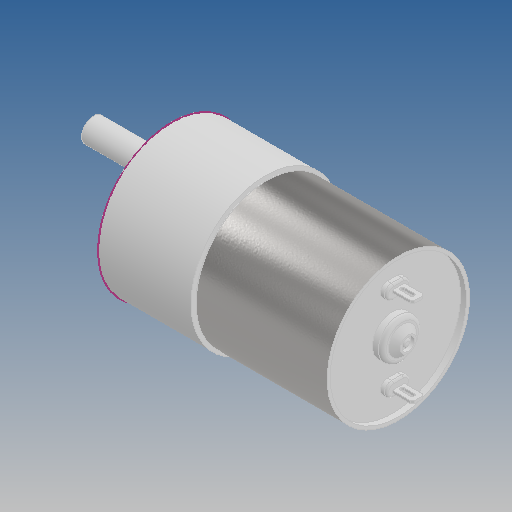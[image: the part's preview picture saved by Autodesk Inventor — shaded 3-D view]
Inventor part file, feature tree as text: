
AUTODESK INVENTOR PART (.ipt)
format: ipt  version: 2020 (Build 240168000, 168)  size: 312,832 bytes
history: native  units: mm
features: other x4, sketch x2
ambient origin geometry x8: Origin, YZ Plane, XZ Plane, XY Plane, X Axis, Y Axis, Z Axis, Center Point
bodies: Body1 (feature_tree)
feature tree (6):
  other  "dc_gear_motor_12V_500rpm.ipt"
  other  "Solid1::dc_gear_motor_12V_500rpm.ipt"
  other  "Элемент создания тегов1"
  sketch  "Sketch1"  dims[d0=10.0mm]
  sketch  "Sketch2"
  other  "Твердое тело1"
